# Revit family: Indirect-Water-Heater_AO_Smith-IT-300_B_B
name_source: partatom
category: Mechanical Equipment
revit_build: Autodesk Revit 2016 (Build: 20170117_1200(x64)
units: mm (PartAtom-declared; Revit-internal decimal feet)

## family parameters
Always vertical = Yes
Cut with Voids When Loaded = No
OmniClass Number = 23.75.00.00
OmniClass Title = Climate Control (HVAC)
Part Type = Normal
Room Calculation Point = No
Round Connector Dimension = Use Radius
Shared = No
Work Plane-Based = No

## types (1)
- IT 300 B B
    1e Maintenance (check-up) = 3 maanden na installatie
    2nd Maintenance (general maintenance) = 12 maanden na installatie
    Assembly Code = D3010
    BIM Content Developer = CAD & Company
    BIM Content Developer URL = http://www.cadcompany.be
    Category = Mechanical Equipment
    Cold Water Connection R = 1"
    Description = Indirecte Boiler met 1 warmtewisselaar
    Destination / Counrty = België
    Diameter (with insulation) = 750 mm  [stored 2.46063 ft]
    Diameter (without insulation) = 550 mm  [stored 1.80446 ft]
    Draw-off Capacity @ ΔT = 28°C after 120 min. = 3347.0 L
    Draw-off Capacity @ ΔT = 28°C after 30 min. = 1228.0 L
    Draw-off Capacity @ ΔT = 28°C after 60 min. = 1934.0 L
    Draw-off Capacity @ ΔT = 28°C after 90 min. = 2641.0 L
    Draw-off Capacity @ ΔT = 44°C after 120 min. = 2130.0 L
    Draw-off Capacity @ ΔT = 44°C after 30 min. = 781.0 L
    Draw-off Capacity @ ΔT = 44°C after 60 min. = 1231.0 L
    Draw-off Capacity @ ΔT = 44°C after 90 min. = 1680.0 L
    Draw-off Capacity @ ΔT = 50°C after 120 min. = 1874.0 L
    Draw-off Capacity @ ΔT = 50°C after 30 min. = 688.0 L
    Draw-off Capacity @ ΔT = 50°C after 60 min. = 1083.0 L
    Draw-off Capacity @ ΔT = 50°C after 90 min. = 1479.0 L
    Draw-off Capacity @ ΔT = 55°C after 120 min. = 1704.0 L
    Draw-off Capacity @ ΔT = 55°C after 30 min. = 625.0 L
    Draw-off Capacity @ ΔT = 55°C after 60 min. = 985.0 L
    Draw-off Capacity @ ΔT = 55°C after 90 min. = 1344.0 L
    Draw-off Capacity @ ΔT = 70°C after 120 min. = 1339.0 L
    Draw-off Capacity @ ΔT = 70°C after 30 min. = 491.0 L
    Draw-off Capacity @ ΔT = 70°C after 60 min. = 774.0 L
    Draw-off Capacity @ ΔT = 70°C after 90 min. = 1056.0 L
    Empty Weight = 125.00 kg
    Flow Rate - Volume L/h = 1978
    Heating Up Time @ ΔT = 28°C = 13
    Heating Up Time @ ΔT = 44°C = 20
    Heating Up Time @ ΔT = 50°C = 22
    Heating Up Time @ ΔT = 55°C = 25
    Heating Up Time @ ΔT = 70°C = 31
    Height (with insulation) = 1650 mm  [stored 5.41339 ft]
    Height (without insulation) = 1545 mm  [stored 5.0689 ft]
    Height Cold Water Inlet = 110 mm  [stored 0.360892 ft]
    Height Warm Water Outlet = 1460 mm  [stored 4.79003 ft]
    Host = Unhosted
    Hot / Warm Water Connection R = 1"
    Insulation Thickness = 100 mm  [stored 0.328084 ft]
    Maintenance Interval = 12 maanden
    Manufacturer = A.O. Smith Water Products Company b.v.
    Manufacturer Number = E 7110
E 7110
E 7110
    Max. Operating Pressure - bottom heat exchanger = 2500000.0 Pa
    Max. Operating Pressure - tank = 1000000.0 Pa
    Max. Tempature - bottom heat exchanger = 110 °C
    Max. Temperature - tank = 95 °C
    Model = IT 300 B B
    NLSfB = 51.11
    Nominal Output - bottom heat exchanger = 46000 W
    Operating Weight = 425.00 kg
    Packaging Height = 1770 mm  [stored 5.80709 ft]
    Packaging Length = 800 mm  [stored 2.62467 ft]
    Packaging Width = 800 mm  [stored 2.62467 ft]
    Pressure Loss - bottom heat exchanger 80ºC/60ºC = 5600.0 Pa
    Product Documentation Link = https://www.aosmithinternational.com
    Product Instruction Link = https://www.aosmithinternational.com
    Productcode = 8717449181772
    Productversion = 1.0
    Recovery Rate @ ΔT = 28°C (ltr/hr) = 1413
    Recovery Rate @ ΔT = 44°C (ltr/hr) = 899
    Recovery Rate @ ΔT = 50°C (ltr/hr) = 791
    Recovery Rate @ ΔT = 55°C (ltr/hr) = 719
    Recovery Rate @ ΔT = 70°C (ltr/hr) = 565
    Serial Number = 8717449181772
    Stand-by Loss = 0 W
    Stand-by Loss - daily (Watt/24H) = 0
    Storage Capacity - bottom heat exchanger = 8.9 m³
    Storage Capacity - tank = 300 m³
    Surface bottom heat Exchanger = 1.47 m²
    T&P Connection Rp = 1"
    Transport Weight = 133.00 kg
    Type of Packaging = Plastic en Hout
    URL = www.aosmith.be
    Warranty on Parts = 12 maanden
    Warranty on Tank = 36 maanden
    Workspace Diameter = 1750 mm  [stored 5.74147 ft]
    Workspace Height = 2650 mm  [stored 8.69423 ft]

note: [stored X ft] marks values corroborated as IEEE doubles in the binary element streams (Revit-internal decimal feet)

## geometry (parser evidence)
native form markers: Blend x2, Sweep x21
no freeform markers — native parametric forms only
